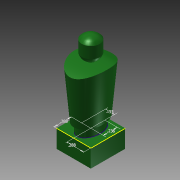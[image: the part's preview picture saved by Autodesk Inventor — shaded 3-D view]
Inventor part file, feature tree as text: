
AUTODESK INVENTOR PART (.ipt)
format: ipt  version: 2015 (Build 190159000, 159)  size: 190,976 bytes
history: native  units: in
note: dims shown in document units (in); Inventor stores cm internally (conversion verified against a paired STEP export)
features: sketch x5, extrude x4, projected_geometry x2, plane x1, revolve x1
ambient origin geometry x8: Origin, YZ Plane, XZ Plane, XY Plane, X Axis, Y Axis, Z Axis, Center Point
bodies: Solid1 (feature_tree)
feature tree (13):
  extrude  "Extrusion1"  Depth=0.575in
  sketch  "Sketch2"  dims[d2=0.3in d3=0.0in d4=0.2875in]
  extrude  "Extrusion2"  Depth=0.2875in
  extrude  "Extrusion3"  Depth=0.236in
  plane  "Work Plane2"
  extrude  "Extrusion4"  Depth=0.155in TaperAngle=0.0deg
  revolve  "Revolution1"  [1 undecoded]
  sketch  "Sketch1"  dims[d0=0.575in d1=0.575in]
  sketch  "Sketch3"  dims[d5=0.2875in d6=0.236in]
  sketch  "Sketch4"  dims[d7=0.155in d8=0.155in d9=0.0in]
  sketch  "Sketch5"  dims[d10=0.2875in d11=0.2875in d12=0.286in d13=0.205in d14=0.84in d15=0.0344in d16=1.2in d17=0.6in d18=1.05in d19=1.0in d20=0.0in d21=90.0deg]
  projected_geometry  "Projected Loop1"
  projected_geometry  "Projected Loop2"
note: 1 required parameter value undecoded (feature->parameter linkage not recoverable at this tier; creation-order binding heuristic only, values carry confidence <= 0.55)
